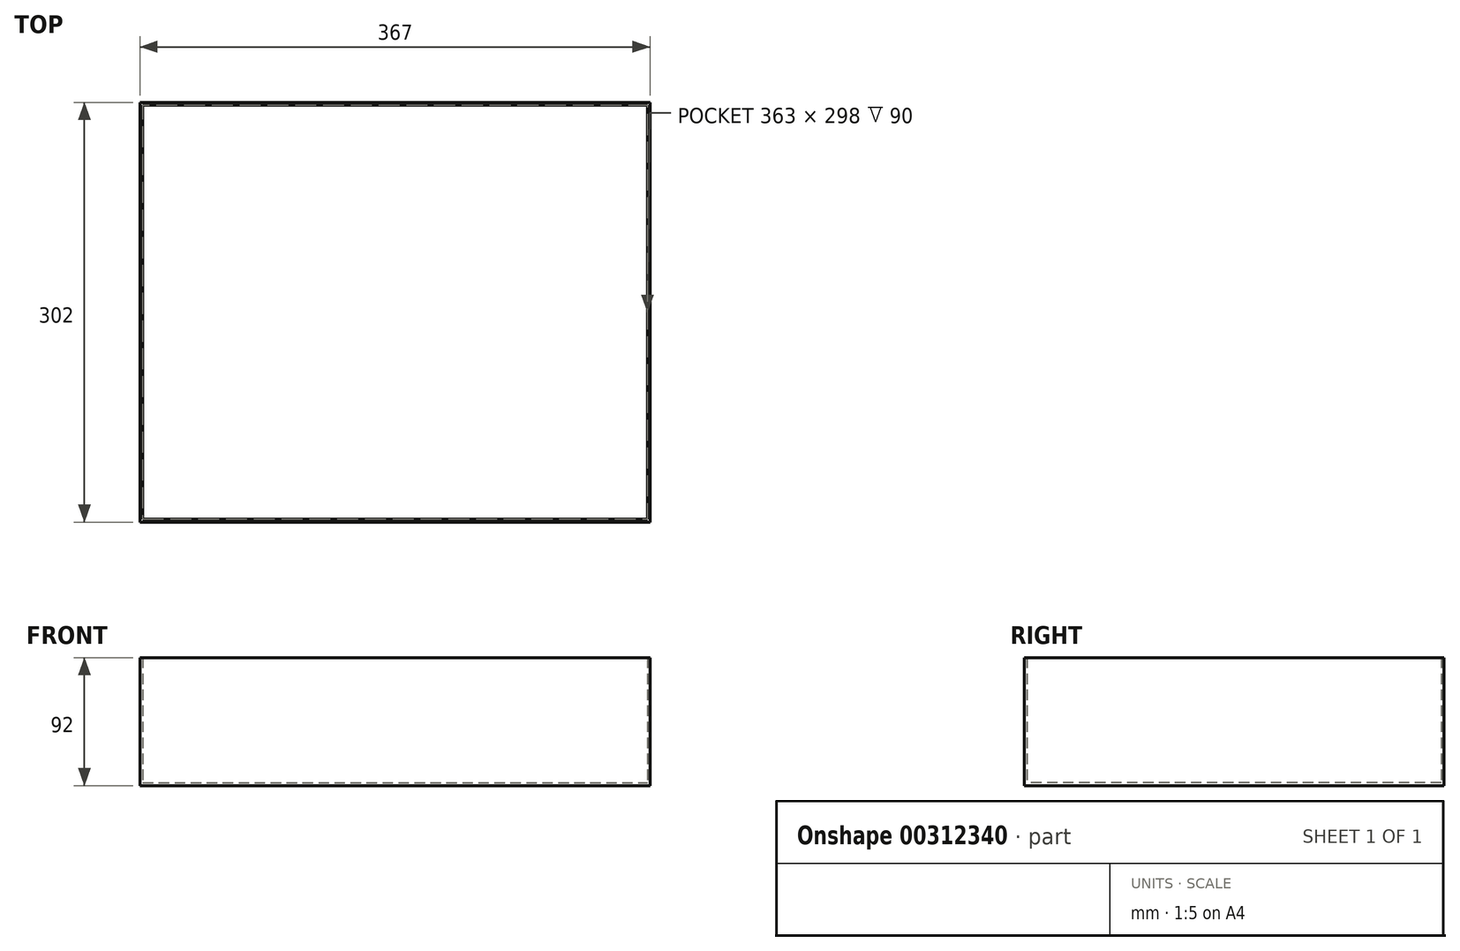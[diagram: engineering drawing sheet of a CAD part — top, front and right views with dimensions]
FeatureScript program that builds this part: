
annotation { "Feature Type Name" : "Feature", "Feature Type Description" : "" }
export const myFeature = defineFeature(function(context is Context, id is Id, definition is map)
    precondition{}
    {
        {
            assignVariable(context, id + "F0", {"name" : "BoxHeight", "anyValue" : 92 * mm});
        }
        {
            var Q0;
            Q0=qCreatedBy(makeId("Top.planeOp"),FACE);
            var sketch = newSketch(context, id + "F1", { "sketchPlane" : qUnion([Q0])});
            skLineSegment(sketch, "E0.bottom", {"start": v(-183.5, 151) * mm, "end": v(183.5, 151) * mm});
            skLineSegment(sketch, "E0.top", {"start": v(-183.5, -151) * mm, "end": v(183.5, -151) * mm});
            skLineSegment(sketch, "E0.left", {"start": v(-183.5, 151) * mm, "end": v(-183.5, -151) * mm});
            skLineSegment(sketch, "E0.right", {"start": v(183.5, 151) * mm, "end": v(183.5, -151) * mm});
            skPoint(sketch, "E0.middle", {"position": v(0, 0) * mm});
            skLineSegment(sketch, "E1.0", {"start": v(-181.5, 149) * mm, "end": v(181.5, 149) * mm});
            skLineSegment(sketch, "E1.1", {"start": v(-181.5, 149) * mm, "end": v(-181.5, -149) * mm});
            skLineSegment(sketch, "E1.2", {"start": v(-181.5, -149) * mm, "end": v(181.5, -149) * mm});
            skLineSegment(sketch, "E1.3", {"start": v(181.5, 149) * mm, "end": v(181.5, -149) * mm});
            skSolve(sketch);
        }
        {
            var Q0;
            Q0=makeQuery(id+"F1.imprint","IMPRINT",FACE,{"disambiguationData":[TD([[makeQuery(id+"F1.imprint","IMPRINT",EDGE,{"derivedFrom":sQuery(id+"F1.wireOp",EDGE,"E0.bottom")}),-1.0]])]});
            extrude(context, id + "F2", {"entities" : qUnion([Q0]), "depth" : getVariable(context, 'BoxHeight')});
        }
        {
            var Q0;
            Q0=qSketchRegion(id+"F1",true);
            var Q1;
            Q1=makeQuery(id+"F1.imprint","IMPRINT",FACE,{"disambiguationData":[TD([[makeQuery(id+"F1.imprint","IMPRINT",EDGE,{"derivedFrom":sQuery(id+"F1.wireOp",EDGE,"E1.0")}),-1.0]])]});
            extrude(context, id + "F3", {"entities" : qUnion([Q0, Q1]), "operationType" : NewBodyOperationType.ADD, "depth" : 2 * mm});
        }
        {
            var Q0;
            Q0=makeQuery(id+"F2.opExtrude","SWEPT_FACE",FACE,{"disambiguationData":[OSD([sQuery(id+"F1.wireOp",EDGE,"E0.top")])]});
            var sketch = newSketch(context, id + "F4", { "sketchPlane" : qUnion([Q0])});
            skLineSegment(sketch, "E2", {"start": v(0, 92) * mm, "end": v(0, 0) * mm, "construction": true});
            skLineSegment(sketch, "E3", {"start": v(0, 46) * mm, "end": v(-50, 46) * mm, "construction": true});
            skLineSegment(sketch, "E4.MirrorCS", {"start": v(0, 46) * mm, "end": v(50, 46) * mm, "construction": true});
            skCircle(sketch, "E5", {"center": v(-50, 46) * mm, "radius": 2.5 * mm});
            skSolve(sketch);
        }
        {
            var Q0;
            Q0=sQuery(id+"F4.wireOp",EDGE,"E3");
            cPlane(context, id + "F5", {"entities" : qUnion([Q0]), "cplaneType" : CPlaneType.LINE_ANGLE, "offset" : 25 * mm, "angle" : 90 * degree, "width" : 150 * mm, "height" : 150 * mm});
        }
    });
